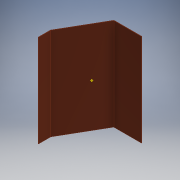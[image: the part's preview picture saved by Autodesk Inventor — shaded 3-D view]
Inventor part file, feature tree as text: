
AUTODESK INVENTOR PART (.ipt)
format: ipt  version: 2018 (Build 220112000, 112)  size: 114,688 bytes
history: native  units: mm
features: sheet_metal_op x3, other x2, sketch x1
ambient origin geometry x8: Origin, YZ Plane, XZ Plane, XY Plane, X Axis, Y Axis, Z Axis, Center Point
bodies: Solid1 (feature_tree)
feature tree (6):
  sheet_metal_op  "Contour Flange1"
  other  "Work Point1"
  sketch  "Sketch1"  dims[d0=300.0mm d1=500.0mm d2=120.0deg d3=5.0mm d4=5.0mm d5=2.5mm d6=10.0mm d7=5.0mm d8=1000.0mm d9=5.0mm d10=5.0mm d11=20.0mm d12=5.0mm d13=5.0mm]
  other  "Plate1"
  sheet_metal_op  "Bend1"
  sheet_metal_op  "Corner1"
